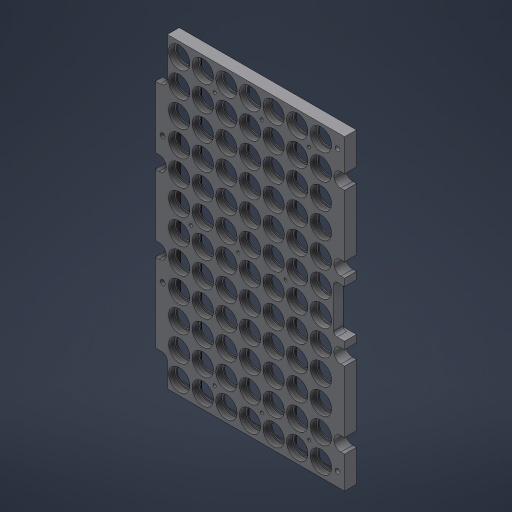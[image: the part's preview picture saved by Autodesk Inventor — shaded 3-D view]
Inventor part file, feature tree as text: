
AUTODESK INVENTOR PART (.ipt)
format: ipt  version: 2024.3 (Build 283343010, 343A)  size: 926,720 bytes
history: native  units: mm
features: extrude x5, sketch x4, hole x4, pattern_linear x1, fillet x1
ambient origin geometry x8: Origin, YZ Plane, XZ Plane, XY Plane, X Axis, Y Axis, Z Axis, Center Point
bodies: Volumenkörper1 (feature_tree)
feature tree (15):
  sketch  "Skizze1"  dims[d0=160.0mm d1=260.0mm]
  extrude  "Extrusion1"  Depth=260.0mm
  hole  "Bohrung1"  [1 undecoded]
  pattern_linear  "Rechteckige Anordnung1"  Count1=6 Spacing1=43.0mm
  sketch  "Skizze2"  dims[d2=10.0mm d3=0.0mm d4=18.0mm d5=60.0mm d7=43.0mm d8=70.0mm d10=20.0mm]
  extrude  "Extrusion4"  Depth=20.0mm
  hole  "Bohrung4"  [1 undecoded]
  sketch  "Skizze4"  dims[d16=21.5mm d19=70.0mm d21=20.0mm]
  extrude  "Extrusion6"  Depth=20.0mm
  extrude  "Extrusion7"  TaperAngle=0.0deg  [1 undecoded]
  fillet  "Rundung3"  Radius=10.0mm
  sketch  "Skizze6"  dims[d22=60.0mm d24=43.0mm d69=15.0mm d70=15.0mm d71=6.0mm d72=18.0mm d73=5.0mm d74=90.0deg d75=8.0mm d76=20.594885mm d77=70.0mm d79=20.0mm d80=0.0mm d83=10.0mm d84=5.0mm d85=60.0mm d101=25.0mm d113=157.7mm d119=8.0mm d121=6.0mm d124=33.25mm d125=64.5mm d126=6.0mm d127=10.75mm d129=7.0mm d130=7.0mm d132=3.0mm d134=10.75mm d135=9.5mm d136=3.0mm d140=10.0mm d141=0.0mm d142=6.0mm d143=4.0mm d144=5.0mm d145=4.0mm d146=6.0mm d147=4.0mm d148=2.0mm d149=90.0deg d150=8.0mm d151=20.594885mm d152=4.0mm d153=6.0mm d154=6.0mm d155=5.0mm d156=90.0deg d157=8.0mm d158=20.594885mm d160=8.0mm d162=3.0mm d165=20.0mm d166=5.75mm d169=7.0mm d170=7.0mm d171=3.64mm d172=10.75mm d180=2.0mm d181=2.0mm d182=5.0mm d184=8.75mm d185=8.75mm d186=4.0mm d187=0.0mm d190=40.0mm d191=20.0mm d192=0.0mm d193=0.0mm d195=60.0mm d196=60.0mm d197=2.0mm d198=3.0mm d199=2.5mm d200=5.0mm d201=17.5mm d202=37.5mm d203=1.25mm d204=30.0mm d206=40.0mm d207=10.0mm d209=10.0mm d211=2.0mm d212=0.0mm d213=40.0mm d214=40.0mm d215=18.75mm d216=107.5mm d217=107.5mm d218=2.5mm d219=6.0mm d220=4.0mm d221=2.0mm d222=90.0deg d223=8.0mm d224=20.594885mm d118=0.5mm d120=0.5mm]
  extrude  "Extrusion8"  Depth=5.0mm
  hole  "Bohrung5"  [1 undecoded]
  hole  "Bohrung3"  [1 undecoded]
note: 5 required parameter values undecoded (feature->parameter linkage not recoverable at this tier; creation-order binding heuristic only, values carry confidence <= 0.55)
